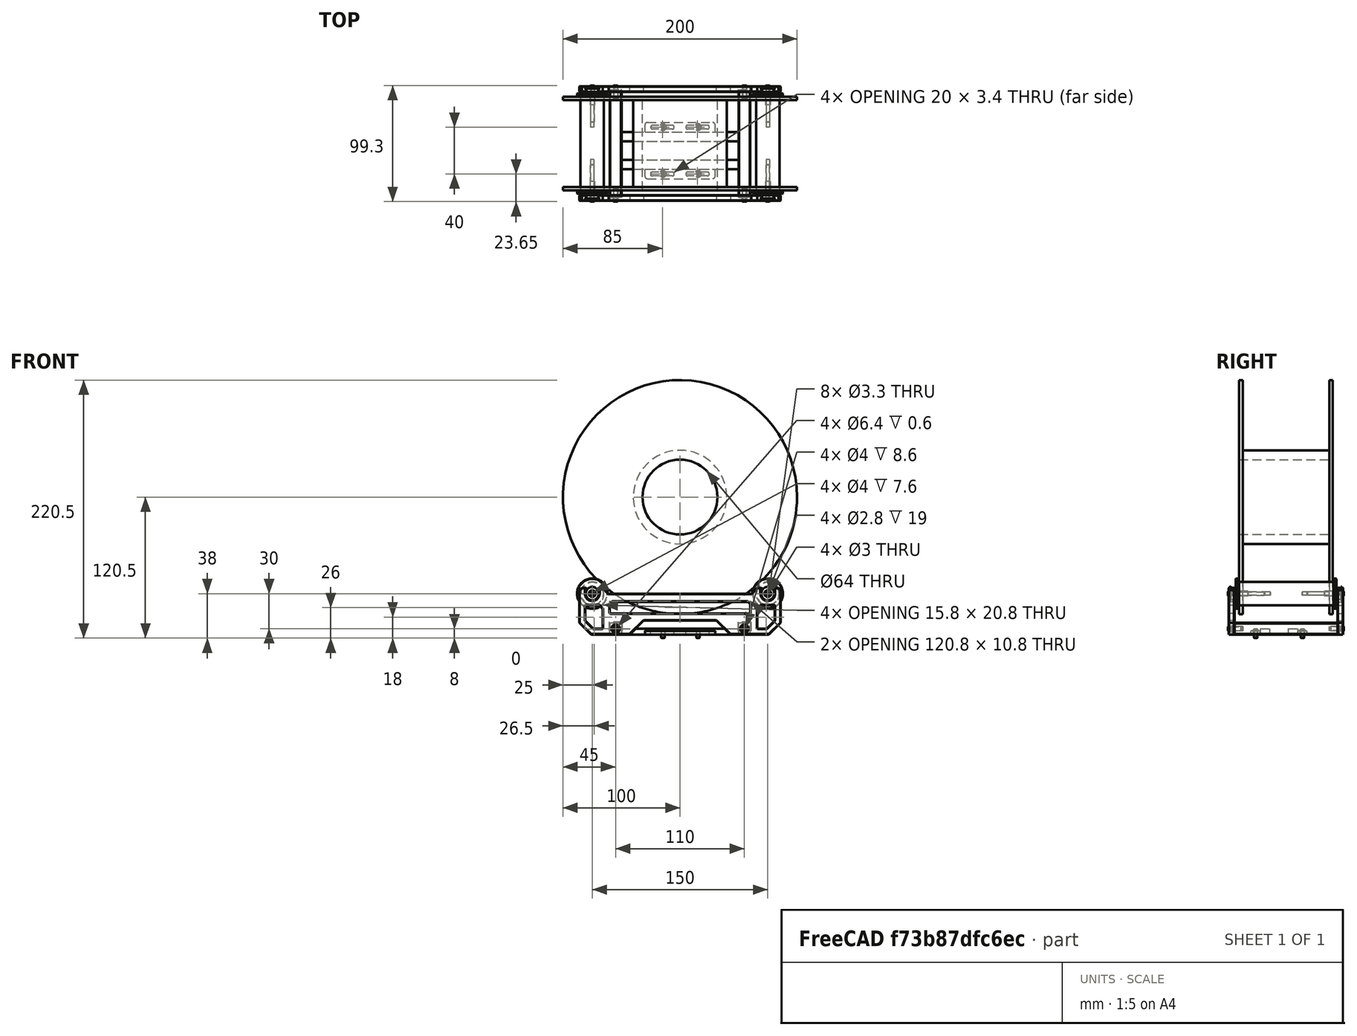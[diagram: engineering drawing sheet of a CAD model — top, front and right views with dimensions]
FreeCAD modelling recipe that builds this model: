
FCSTD DOCUMENT  (FreeCAD 0.19R24291 (Git))
Label: filament-spool-holder-assembly
License: Other
LicenseURL: GPL3
objects: Part::Feature×14, Part::FeaturePython×12, App::Part×1
note: 26 computed .brp shape members not serialized (recipe doc carries the construction recipe); baked Part::Feature solids carry a one-line shape summary decoded from their .brp

FEATURE [Part::Feature] Chamfer004013007011015006009007001065001001  label="ladder002"
  shape: bbox 120 x 92 x 10 mm, 79 faces (baked)
FEATURE [Part::Feature] Cut002002002002006  label="filament-spoll"
  Placement = pos=(0,-40,117.5) rot=(-1,0,0;1.5708rad)
  shape: bbox 200 x 80 x 200 mm, 8 faces (baked)
FEATURE [Part::FeaturePython] Screw004  label="M3x6-Screw"  # Fasteners workbench fastener (typed FeaturePython)
  Placement = pos=(-14.6,14.1,3) rot=(0,0,1;0rad)
  diameter = 1
  invert = false
  length = 0
  lengthCustom = 6
  matchOuter = true
  offset = 0
  thread = false
  type = 39
FEATURE [Part::FeaturePython] Screw005  label="M3x6-Screw007"  # Fasteners workbench fastener (typed FeaturePython)
  Placement = pos=(-14.6,-25.9,3) rot=(0,0,1;0rad)
  diameter = 1
  invert = false
  length = 0
  lengthCustom = 6
  matchOuter = true
  offset = 0
  thread = false
  type = 39
FEATURE [Part::FeaturePython] Screw006  label="M3x6-Screw009"  # Fasteners workbench fastener (typed FeaturePython)
  Placement = pos=(15.4,-25.9,3) rot=(0,0,1;0rad)
  diameter = 1
  invert = false
  length = 0
  lengthCustom = 6
  matchOuter = true
  offset = 0
  thread = false
  type = 39
FEATURE [Part::FeaturePython] Screw007  label="M3x6-Screw008"  # Fasteners workbench fastener (typed FeaturePython)
  Placement = pos=(15.4,14.1,3) rot=(0,0,1;0rad)
  diameter = 1
  invert = false
  length = 0
  lengthCustom = 6
  matchOuter = true
  offset = 0
  thread = false
  type = 39
FEATURE [Part::Feature] Cut008004003004014002002005003004003002003021022001002001105001001  label="F623-bearing002"
  Placement = pos=(-75,-48,35) rot=(1,0,0;4.71239rad)
  shape: bbox 11.5 x 4 x 11.5 mm, 6 faces (baked)
FEATURE [Part::Feature] Chamfer004013007011015006009007001081001001  label="plate-r003"
  Placement = pos=(0,-1,0) rot=(0,0,1;0rad)
  shape: bbox 172 x 5 x 40 mm, 230 faces (baked)
FEATURE [Part::Feature] Chamfer004013007011015006009007001082001002  label="plate-r004"
  Placement = pos=(2e-16,1,0) rot=(0,0,1;3.14159rad)
  shape: bbox 172 x 5 x 40 mm, 230 faces (baked)
FEATURE [Part::Feature] Cut008004003004014002002005003004003002003021022001002001105001002  label="F623-bearing003"
  Placement = pos=(75,-48,35) rot=(-1,0,0;1.5708rad)
  shape: bbox 11.5 x 4 x 11.5 mm, 6 faces (baked)
FEATURE [Part::Feature] Cut008004003004014002002005003004003002003021022001002001105001003  label="F623-bearing004"
  Placement = pos=(75,48,35) rot=(0,0.707107,-0.707107;3.14159rad)
  shape: bbox 11.5 x 4 x 11.5 mm, 6 faces (baked)
FEATURE [Part::Feature] Cut008004003004014002002005003004003002003021022001002001105001004  label="F623-bearing005"
  Placement = pos=(-75,48,35) rot=(0,0.707107,-0.707107;3.14159rad)
  shape: bbox 11.5 x 4 x 11.5 mm, 6 faces (baked)
FEATURE [Part::Feature] Chamfer004013007011015006009007001083001001  label="stopper002"
  Placement = pos=(-75,-41,35) rot=(1,0,0;1.5708rad)
  shape: bbox 26 x 3 x 26 mm, 9 faces (baked)
FEATURE [Part::Feature] Chamfer004013007011015006009007001083001002  label="stopper003"
  Placement = pos=(-75,41,35) rot=(0,0.707107,0.707107;3.14159rad)
  shape: bbox 26 x 3 x 26 mm, 9 faces (baked)
FEATURE [Part::Feature] Chamfer004013007011015006009007001083001003  label="stopper004"
  Placement = pos=(75,41,35) rot=(0,0.707107,0.707107;3.14159rad)
  shape: bbox 26 x 3 x 26 mm, 9 faces (baked)
FEATURE [Part::Feature] Chamfer004013007011015006009007001083001004  label="stopper005"
  Placement = pos=(75,-41,35) rot=(-1,0,0;4.71239rad)
  shape: bbox 26 x 3 x 26 mm, 9 faces (baked)
FEATURE [Part::Feature] Chamfer004013007011015006009007001084001  label="roller001"
  Placement = pos=(-75,41,35) rot=(1,0,0;1.5708rad)
  shape: bbox 20 x 81.5 x 20 mm, 15 faces (baked)
FEATURE [Part::Feature] Chamfer004013007011015006009007001083001005  label="roller002"
  Placement = pos=(75,41,35) rot=(1,0,0;1.5708rad)
  shape: bbox 20 x 81.5 x 20 mm, 15 faces (baked)
FEATURE [Part::FeaturePython] Screw  label="M3x30-Screw"  # Fasteners workbench fastener (typed FeaturePython)
  Placement = pos=(-75,-48,35) rot=(1,0,0;1.5708rad)
  baseObject = -> Cut008004003004014002002005003004003002003021022001002001105001001 [Edge9]
  diameter = 1
  invert = true
  length = 8
  lengthCustom = 30
  matchOuter = true
  offset = 0
  thread = false
  type = 39
FEATURE [Part::FeaturePython] Screw008  label="M3x30-Screw001"  # Fasteners workbench fastener (typed FeaturePython)
  Placement = pos=(75,-48,35) rot=(1,0,0;1.5708rad)
  baseObject = -> Cut008004003004014002002005003004003002003021022001002001105001002 [Edge9]
  diameter = 1
  invert = true
  length = 8
  lengthCustom = 30
  matchOuter = true
  offset = 0
  thread = false
  type = 39
FEATURE [Part::FeaturePython] Screw009  label="M3x30-Screw002"  # Fasteners workbench fastener (typed FeaturePython)
  Placement = pos=(75,48,35) rot=(-1,0,0;1.5708rad)
  baseObject = -> Cut008004003004014002002005003004003002003021022001002001105001003 [Edge9]
  diameter = 1
  invert = true
  length = 8
  lengthCustom = 30
  matchOuter = true
  offset = 0
  thread = false
  type = 39
FEATURE [Part::FeaturePython] Screw010  label="M3x30-Screw003"  # Fasteners workbench fastener (typed FeaturePython)
  Placement = pos=(-75,48,35) rot=(-1,0,0;1.5708rad)
  baseObject = -> Cut008004003004014002002005003004003002003021022001002001105001004 [Edge9]
  diameter = 1
  invert = true
  length = 8
  lengthCustom = 30
  matchOuter = true
  offset = 0
  thread = false
  type = 39
FEATURE [Part::FeaturePython] Screw011  label="M3x10-Screw"  # Fasteners workbench fastener (typed FeaturePython)
  Placement = pos=(55,48,5) rot=(-1,0,0;1.5708rad)
  baseObject = -> Chamfer004013007011015006009007001081001001 [Edge534]
  diameter = 1
  invert = true
  length = 2
  lengthCustom = 10
  matchOuter = true
  offset = 0
  thread = false
  type = 39
FEATURE [Part::FeaturePython] Screw012  label="M3x10-Screw001"  # Fasteners workbench fastener (typed FeaturePython)
  Placement = pos=(-55,48,5) rot=(-1,0,0;1.5708rad)
  baseObject = -> Chamfer004013007011015006009007001081001001 [Edge533]
  diameter = 1
  invert = true
  length = 2
  lengthCustom = 10
  matchOuter = true
  offset = 0
  thread = false
  type = 39
FEATURE [Part::FeaturePython] Screw013  label="M3x10-Screw002"  # Fasteners workbench fastener (typed FeaturePython)
  Placement = pos=(-55,-48,5) rot=(1,0,0;1.5708rad)
  baseObject = -> Chamfer004013007011015006009007001082001002 [Edge534]
  diameter = 1
  invert = true
  length = 2
  lengthCustom = 10
  matchOuter = true
  offset = 0
  thread = false
  type = 39
FEATURE [Part::FeaturePython] Screw014  label="M3x10-Screw003"  # Fasteners workbench fastener (typed FeaturePython)
  Placement = pos=(55,-48,5) rot=(1,0,0;1.5708rad)
  baseObject = -> Chamfer004013007011015006009007001082001002 [Edge533]
  diameter = 1
  invert = true
  length = 2
  lengthCustom = 10
  matchOuter = true
  offset = 0
  thread = false
  type = 39
FEATURE [App::Part] Part  label="spool-holder"
  Group = -> [Chamfer004013007011015006009007001065001001,Cut002002002002006,Screw007,Screw006,Screw005,Screw004,Screw,Cut008004003004014002002005003004003002003021022001002001105001001,Screw011,Screw012,Chamfer004013007011015006009007001081001001,Screw013,Screw014,Chamfer004013007011015006009007001082001002,Screw008,Cut008004003004014002002005003004003002003021022001002001105001002,Screw009,+9 more]
  Origin = -> Origin
